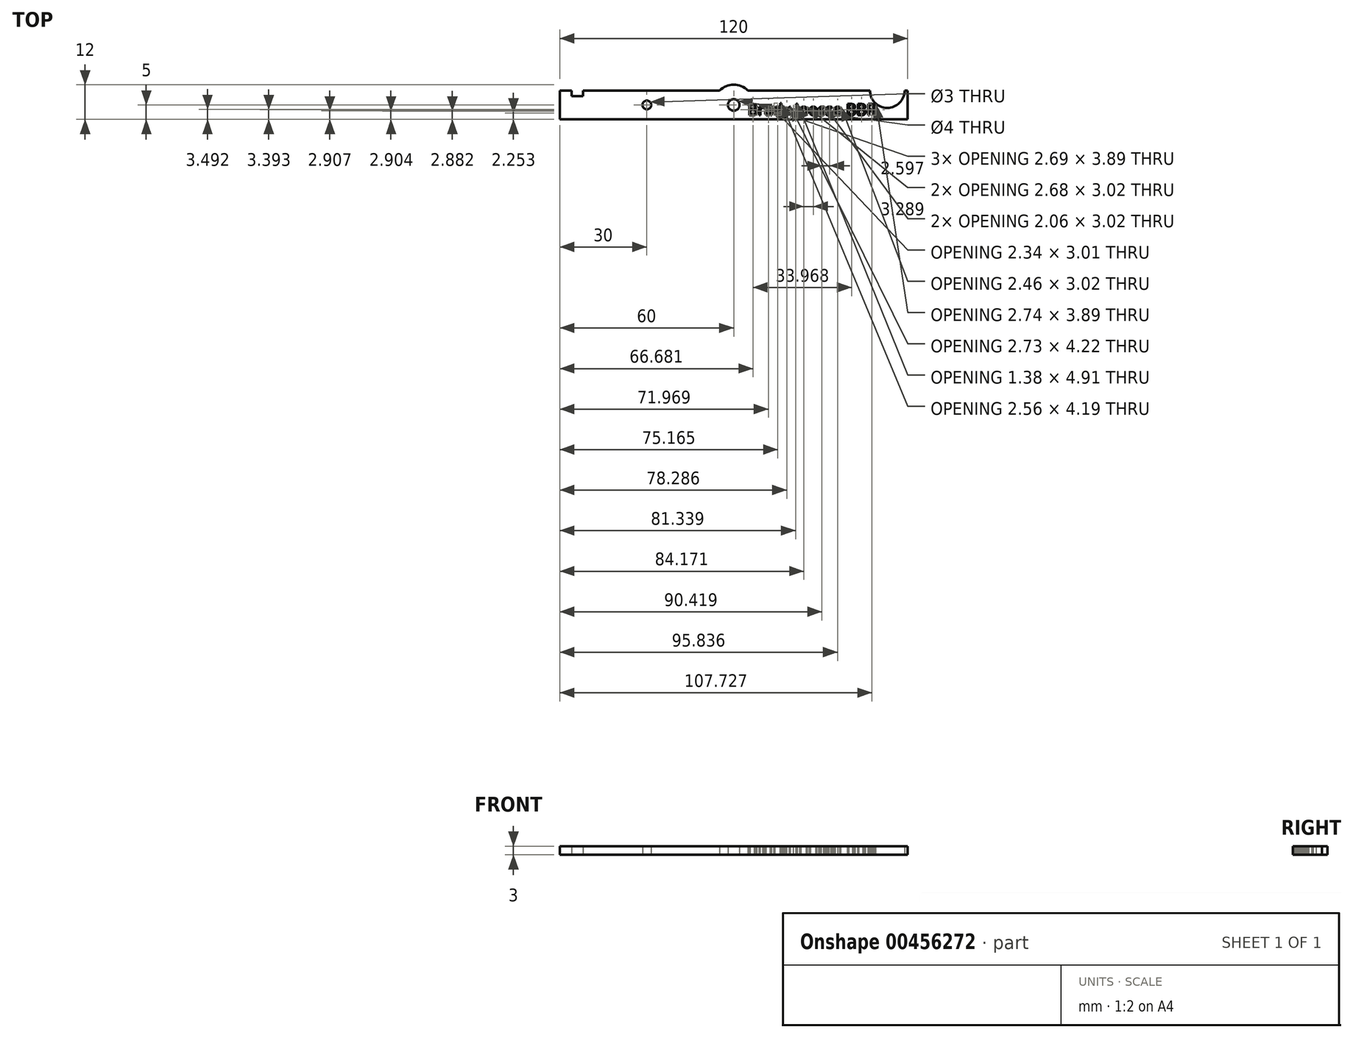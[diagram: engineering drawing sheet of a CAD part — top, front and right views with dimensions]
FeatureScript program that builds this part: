
annotation { "Feature Type Name" : "Feature", "Feature Type Description" : "" }
export const myFeature = defineFeature(function(context is Context, id is Id, definition is map)
    precondition{}
    {
        {
            var Q0;
            Q0=qCreatedBy(makeId("Top.planeOp"),FACE);
            var sketch = newSketch(context, id + "F0", { "sketchPlane" : qUnion([Q0])});
            skLineSegment(sketch, "E0.bottom", {"start": v(-60, -5) * mm, "end": v(60, -5) * mm});
            skLineSegment(sketch, "E0.top", {"start": v(-60, 5) * mm, "end": v(60, 5) * mm});
            skLineSegment(sketch, "E0.left", {"start": v(-60, -5) * mm, "end": v(-60, 5) * mm});
            skLineSegment(sketch, "E0.right", {"start": v(60, -5) * mm, "end": v(60, 5) * mm});
            skPoint(sketch, "E0.middle", {"position": v(0, 0) * mm});
            skLineSegment(sketch, "E1.bottom", {"start": v(-56, 5) * mm, "end": v(-52, 5) * mm});
            skLineSegment(sketch, "E1.top", {"start": v(-56, 3) * mm, "end": v(-52, 3) * mm});
            skLineSegment(sketch, "E1.left", {"start": v(-56, 5) * mm, "end": v(-56, 3) * mm});
            skLineSegment(sketch, "E1.right", {"start": v(-52, 5) * mm, "end": v(-52, 3) * mm});
            skCircle(sketch, "E2", {"center": v(0, 0) * mm, "radius": 2 * mm});
            skCircle(sketch, "E3", {"center": v(0, 0) * mm, "radius": 7 * mm});
            skCircle(sketch, "E4", {"center": v(53, 5) * mm, "radius": 6 * mm});
            skCircle(sketch, "E5", {"center": v(-30, 0) * mm, "radius": 1.5 * mm});
            skSolve(sketch);
        }
        {
            var Q0;
            {var subQ0=sQuery(id+"F0.wireOp",EDGE,"E0.left");Q0=makeQuery(id+"F0.imprint","IMPRINT",FACE,{"disambiguationData":[TD([[makeQuery(id+"F0.imprint","IMPRINT",EDGE,{"derivedFrom":subQ0}),-1.0]])]});}
            var Q1;
            {var subQ0=sQuery(id+"F0.wireOp",EDGE,"E0.right");Q1=makeQuery(id+"F0.imprint","IMPRINT",FACE,{"disambiguationData":[TD([[makeQuery(id+"F0.imprint","IMPRINT",EDGE,{"derivedFrom":subQ0}),1.0]])]});}
            var Q2;
            {var subQ0=sQuery(id+"F0.wireOp",EDGE,"E3");var subQ1=sQuery(id+"F0.wireOp",EDGE,"E0.bottom");var subQ2=makeQuery(id+"F0.imprint","INTERSECT",VERTEX,{"disambiguationData":[OD(0.0)],"derivedFrom":[subQ1,subQ0]});Q2=makeQuery(id+"F0.imprint","IMPRINT",FACE,{"disambiguationData":[TD([[makeQuery(id+"F0.imprint","IMPRINT",EDGE,{"disambiguationData":[TD([[subQ2,-1.0]])],"derivedFrom":subQ1}),-1.0]])]});}
            var Q3;
            Q3=makeQuery(id+"F0.imprint","IMPRINT",FACE,{"disambiguationData":[TD([[makeQuery(id+"F0.imprint","IMPRINT",EDGE,{"derivedFrom":sQuery(id+"F0.wireOp",EDGE,"E2")}),-1.0]])]});
            var Q4;
            {var subQ0=sQuery(id+"F0.wireOp",EDGE,"E3");var subQ1=sQuery(id+"F0.wireOp",EDGE,"E0.top");var subQ2=makeQuery(id+"F0.imprint","INTERSECT",VERTEX,{"disambiguationData":[OD(0.0)],"derivedFrom":[subQ1,subQ0]});Q4=makeQuery(id+"F0.imprint","IMPRINT",FACE,{"disambiguationData":[TD([[makeQuery(id+"F0.imprint","IMPRINT",EDGE,{"disambiguationData":[TD([[subQ2,-1.0]])],"derivedFrom":subQ1}),1.0]])]});}
            extrude(context, id + "F1", {"entities" : qUnion([Q0, Q1, Q2, Q3, Q4]), "depth" : 3 * mm});
        }
        {
            var Q0;
            Q0=makeQuery(id+"F1.opExtrude","CAP_FACE",FACE,{"disambiguationData":[OSD([sQuery(id+"F0.wireOp",EDGE,"E0.bottom"),sQuery(id+"F0.wireOp",EDGE,"E0.top"),sQuery(id+"F0.wireOp",EDGE,"E0.left"),sQuery(id+"F0.wireOp",EDGE,"E0.right"),sQuery(id+"F0.wireOp",EDGE,"E1.top"),sQuery(id+"F0.wireOp",EDGE,"E1.left"),sQuery(id+"F0.wireOp",EDGE,"E1.right"),sQuery(id+"F0.wireOp",EDGE,"E2"),sQuery(id+"F0.wireOp",EDGE,"E3"),sQuery(id+"F0.wireOp",EDGE,"E4"),sQuery(id+"F0.wireOp",EDGE,"E5")])],"isStart":false});
            var sketch = newSketch(context, id + "F2", { "sketchPlane" : qUnion([Q0])});
            skText(sketch, "E6", { "text": "Brady Joosse BBR\n", "fontName": "OpenSans-Regular.ttf"});
            const initialGuessF2  = {"E6": [0.0048, -0.00355, 1, 0, 0.00392]};
            skSetInitialGuess(sketch, initialGuessF2);
            skSolve(sketch);
        }
        {
            var Q0;
            Q0 = qSketchRegion(id + "F2", true);
            extrude(context, id + "F3", {"entities" : qUnion([Q0]), "operationType" : NewBodyOperationType.REMOVE, "oppositeDirection" : true, "depth" : 25 * mm});
        }
    });
